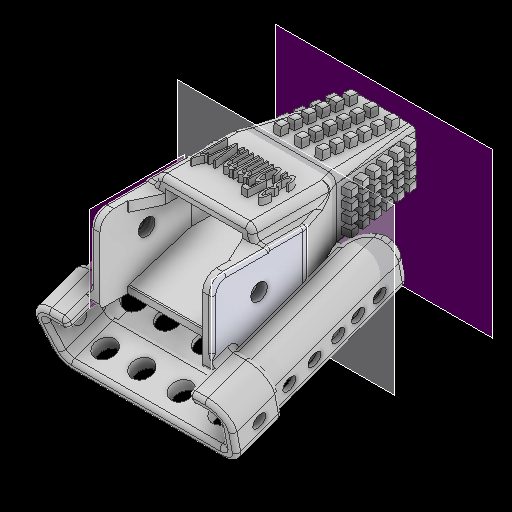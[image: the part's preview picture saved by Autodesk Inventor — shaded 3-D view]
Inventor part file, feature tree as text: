
AUTODESK INVENTOR PART (.ipt)
format: ipt  version: 2025 (Build 290162000, 162)  size: 3,169,792 bytes
history: native  units: mm
features: sketch x21, projected_geometry x20, extrude x8, delete_face x8, thicken_offset x8, plane x7, fillet x7, hole x7, other x3, loft x2, split x2, boolean_combine x2, thread x2, mirror x1, pattern_circular x1, emboss x1
ambient origin geometry x8: Origin, YZ Plane, XZ Plane, XY Plane, X Axis, Y Axis, Z Axis, Center Point
bodies: Solid1 (feature_tree), Solid8 (feature_tree), Solid2 (feature_tree), Solid4 (feature_tree), Solid5 (feature_tree), Solid6 (feature_tree), Solid7 (feature_tree)
feature tree (100):
  plane  "Work Plane6"
  loft  "Loft3"
  loft  "Loft4"
  fillet  "Fillet6"  [1 undecoded]
  sketch  "Sketch46"  dims[d284=0.0mm d287=0.45mm]
  extrude  "Grippers"  Depth=2.45mm
  mirror  "Mirror1"
  sketch  "Sketch47"  dims[d288=0.5mm d296=40.0mm d298=2.5mm d299=60.0mm d301=5.0mm d363=0.5mm d364=0.6mm d416=0.6mm d417=0.0mm d425=0.5mm]
  extrude  "FrontGrippers"  TaperAngle=0.0deg  [1 undecoded]
  sketch  "Sketch49"  dims[d426=60.0mm d428=5.0mm d429=10.0mm d431=10.0mm d433=20.0mm d435=1.5mm d436=20.0mm d438=1.5mm]
  extrude  "BackGrippers"  Depth=15.0mm TaperAngle=0.0deg
  plane  "Work Plane13"
  plane  "Work Plane14"
  extrude  "Extrusion16"  Depth=15.0mm TaperAngle=0.0deg
  extrude  "Extrusion19"  Depth=4.75mm
  extrude  "Extrusion21"  Depth=5.25mm
  extrude  "Extrusion22"  Depth=11.5mm
  plane  "Work Plane28"
  plane  "Work Plane29"
  split  "Split1"
  split  "Split2"
  extrude  "Extrusion34"  Depth=0.45mm
  boolean_combine  "Combine1"
  pattern_circular  "Circular Pattern1"  Count=4  [1 undecoded]
  delete_face  "Delete Face1"
  boolean_combine  "Combine2"
  thicken_offset  "Thicken1"
  thicken_offset  "Thicken2"
  thicken_offset  "Thicken3"
  fillet  "Fillet7"  Radius=0.5mm
  fillet  "Fillet8"  Radius=0.6mm
  fillet  "Fillet9"  Radius=0.6mm
  delete_face  "Delete Face2"
  delete_face  "Delete Face3"
  delete_face  "Delete Face4"
  delete_face  "Delete Face5"
  delete_face  "Delete Face6"
  delete_face  "Delete Face7"
  thicken_offset  "Thicken4"
  fillet  "Fillet10"  [1 undecoded]
  fillet  "Fillet11"  Radius=0.5mm
  hole  "Hole1"  [1 undecoded]
  hole  "Hole2"  [1 undecoded]
  hole  "Hole3"  [1 undecoded]
  hole  "Hole4"  [1 undecoded]
  hole  "Hole5"  [1 undecoded]
  hole  "Hole6"  [1 undecoded]
  thicken_offset  "Thicken5"
  thread  "Thread1"  [1 undecoded]
  thicken_offset  "Thicken6"
  thicken_offset  "Thicken7"
  thread  "Thread2"  [1 undecoded]
  thicken_offset  "Thicken8"
  hole  "Hole7"  [1 undecoded]
  delete_face  "Delete Face8"
  emboss  "Emboss1"
  fillet  "Fillet12"  Radius=0.5mm
  plane  "Work Plane4"
  plane  "Work Plane5"
  sketch  "Sketch5"  dims[d30=0.0mm d31=90.0deg d32=0.0mm d33=90.0deg]
  other  "Edges3"
  sketch  "Sketch7"  dims[d126=1.0mm d127=0.0mm d135=15.0mm d136=0.0mm]
  other  "Edges4"
  sketch  "Sketch22"  dims[d140=1.0mm d141=0.0mm d142=15.0mm d143=0.0mm]
  projected_geometry  "Projected Loop8"
  sketch  "Sketch25"  dims[d156=9.5mm d157=4.75mm]
  sketch  "Sketch27"  dims[d158=10.5mm d159=5.25mm]
  sketch  "Sketch28"  dims[d160=12.5mm d162=11.5mm]
  sketch  "Sketch Rectangular Pattern1"  dims[d20=-7.1mm d22=4.5mm]
  sketch  "Sketch Rectangular Pattern2"  dims[d23=3.5mm d24=0.0mm d25=90.0deg d26=0.0mm d27=90.0deg]
  sketch  "Sketch Rectangular Pattern3"  dims[d28=2.85mm d29=2.45mm]
  projected_geometry  "Projected Loop36"
  projected_geometry  "Projected Loop37"
  projected_geometry  "Projected Loop38"
  projected_geometry  "Projected Loop39"
  projected_geometry  "Projected Loop40"
  projected_geometry  "Projected Loop41"
  projected_geometry  "Projected Loop42"
  projected_geometry  "Projected Loop43"
  projected_geometry  "Projected Loop44"
  projected_geometry  "Projected Loop45"
  projected_geometry  "Projected Loop46"
  projected_geometry  "Projected Loop47"
  projected_geometry  "Projected Loop48"
  projected_geometry  "Projected Loop49"
  projected_geometry  "Projected Loop50"
  projected_geometry  "Projected Loop51"
  projected_geometry  "Projected Loop52"
  projected_geometry  "Projected Loop53"
  sketch  "Sketch50"  dims[d441=0.6mm d442=0.0mm]
  projected_geometry  "Projected Loop54"
  other  "Pattern of Solid6:1"
  sketch  "Sketch51"  dims[d444=6.25mm d445=5.75mm]
  sketch  "Sketch52"  dims[d447=0.25mm d448=0.0mm]
  sketch  "Sketch53"  dims[d449=0.0mm d450=7.5mm d451=0.0mm]
  sketch  "Sketch54"  dims[d452=20.0mm d453=3.490659mm d456=10.0mm d457=10.0mm d458=0.5mm]
  sketch  "Sketch55"  dims[d459=0.5mm d460=0.5mm d461=0.5mm]
  sketch  "Sketch56"  dims[d462=2.0mm]
  sketch  "Sketch57"  dims[d463=2.0mm]
  sketch  "Sketch58"  dims[d464=0.5mm d465=2.0mm d466=2.0mm d467=0.3mm d468=0.3mm d469=1.0mm d470=6.0mm d471=3.023mm d472=2.0mm d473=14.3117mm d474=1.0mm d475=0.0mm d476=1.0mm d477=6.0mm d478=4.0mm d479=2.0mm d480=90.0deg d481=1.0mm d482=0.0mm d483=1.0mm d484=6.0mm d485=4.0mm d486=2.0mm d487=90.0deg d488=1.0mm d489=0.0mm d490=1.0mm d491=6.0mm d492=4.0mm d493=2.0mm d494=90.0deg d495=1.0mm d496=0.0mm d497=1.5mm d498=6.0mm d499=4.0mm d500=2.0mm d501=90.0deg d502=1.0mm d503=0.0mm d504=1.5mm d505=6.0mm d506=4.0mm d507=2.0mm d508=90.0deg d509=1.0mm d510=0.0mm d511=0.2mm d512=0.2mm d513=0.7mm d514=0.0mm d515=0.2mm d516=0.2mm d517=0.2mm d518=0.2mm d519=0.7mm d520=0.0mm d521=0.2mm d522=0.2mm d523=4.0mm d524=6.0mm d525=3.023mm d526=2.0mm d527=14.3117mm d528=1.0mm d529=0.0mm d530=0.5mm d531=0.0mm d532=0.05mm d39=0.5mm d40=0.872665mm d41=0.5mm d42=0.872665mm d193=0.5mm d194=0.872665mm d195=0.5mm d196=0.872665mm]
note: 13 required parameter values undecoded (feature->parameter linkage not recoverable at this tier; creation-order binding heuristic only, values carry confidence <= 0.55)
